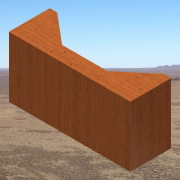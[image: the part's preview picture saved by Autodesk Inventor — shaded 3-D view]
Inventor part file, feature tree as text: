
AUTODESK INVENTOR PART (.ipt)
format: ipt  version: 2013 SP2 (Build 170200200, 200)  size: 132,608 bytes
history: native  units: in
note: dims shown in document units (in); Inventor stores cm internally (conversion verified against a paired STEP export)
features: extrude x1, sketch x1
ambient origin geometry x8: Origin, YZ Plane, XZ Plane, XY Plane, X Axis, Y Axis, Z Axis, Center Point
bodies: Solid1 (feature_tree)
feature tree (2):
  extrude  "Extrusion1"  Depth=8.0in
  sketch  "Sketch1"  dims[d4=8.0in d5=8.0in d6=5.0in d7=1.5in d8=4.0in d9=0.0in]
